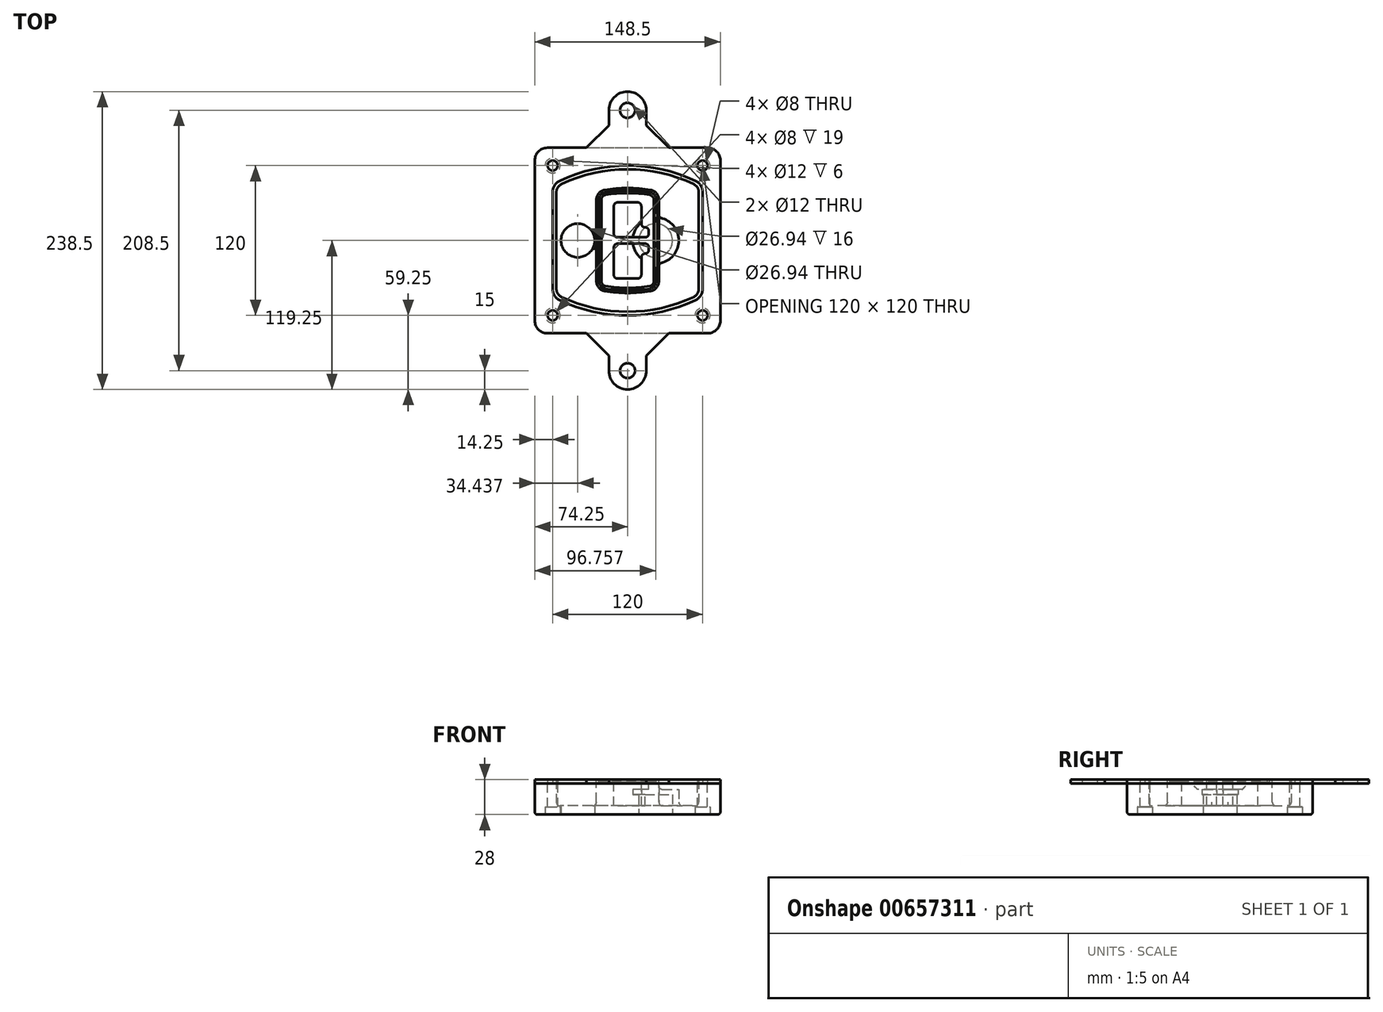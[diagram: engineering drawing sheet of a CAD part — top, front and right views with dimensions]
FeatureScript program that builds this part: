
annotation { "Feature Type Name" : "Feature", "Feature Type Description" : "" }
export const myFeature = defineFeature(function(context is Context, id is Id, definition is map)
    precondition{}
    {
        {
            var Q0;
            Q0=qCreatedBy(makeId("Top.planeOp"),FACE);
            var sketch = newSketch(context, id + "F0", { "sketchPlane" : qUnion([Q0])});
            skPoint(sketch, "E0.rect.middle", {"position": v(0, 0) * mm});
            skLineSegment(sketch, "E1.bottom", {"start": v(-64.25, -74.25) * mm, "end": v(64.25, -74.25) * mm});
            skLineSegment(sketch, "E1.top", {"start": v(-64.25, 74.25) * mm, "end": v(64.25, 74.25) * mm});
            skLineSegment(sketch, "E1.left", {"start": v(-74.25, -64.25) * mm, "end": v(-74.25, 64.25) * mm});
            skLineSegment(sketch, "E1.right", {"start": v(74.25, -64.25) * mm, "end": v(74.25, 64.25) * mm});
            skLineSegment(sketch, "E2", {"start": v(-74.25, 74.25) * mm, "end": v(74.25, -74.25) * mm, "construction": true});
            skLineSegment(sketch, "E3", {"start": v(74.25, 74.25) * mm, "end": v(-74.25, -74.25) * mm, "construction": true});
            skCircle(sketch, "E4", {"center": v(-60, 60) * mm, "radius": 4 * mm});
            skCircle(sketch, "E5", {"center": v(60, 60) * mm, "radius": 4 * mm});
            skCircle(sketch, "E6", {"center": v(60, -60) * mm, "radius": 4 * mm});
            skCircle(sketch, "E7", {"center": v(-60, -60) * mm, "radius": 4 * mm});
            skLineSegment(sketch, "E8", {"start": v(-60, 60) * mm, "end": v(60, 60) * mm, "construction": true});
            skLineSegment(sketch, "E9", {"start": v(60, 60) * mm, "end": v(60, -60) * mm, "construction": true});
            skLineSegment(sketch, "E10", {"start": v(60, -60) * mm, "end": v(-60, -60) * mm, "construction": true});
            skLineSegment(sketch, "E11", {"start": v(-60, -60) * mm, "end": v(-60, 60) * mm, "construction": true});
            skLineSegment(sketch, "E12", {"start": v(-60, 38.83) * mm, "end": v(-60, -38.83) * mm});
            skLineSegment(sketch, "E13", {"start": v(60, 38.83) * mm, "end": v(60, -38.83) * mm});
            skArc(sketch, "E14", {"start": v(54.26, 47.88) * mm, "mid": v(0, 60) * mm, "end": v(-54.26, 47.88) * mm});
            skArc(sketch, "E15", {"start": v(-54.26, -47.88) * mm, "mid": v(0, -60) * mm, "end": v(54.26, -47.88) * mm});
            skLineSegment(sketch, "E16", {"start": v(-60, 0) * mm, "end": v(60, 0) * mm, "construction": true});
            skPoint(sketch, "E17.visualSharp", {"position": v(-60, -45) * mm});
            skArc(sketch, "E17.filletArc", {"start": v(-60, -38.83) * mm, "mid": v(-58.44, -44.2) * mm, "end": v(-54.26, -47.88) * mm});
            skPoint(sketch, "E18.visualSharp", {"position": v(-60, 45) * mm});
            skArc(sketch, "E18.filletArc", {"start": v(-54.26, 47.88) * mm, "mid": v(-58.44, 44.2) * mm, "end": v(-60, 38.83) * mm});
            skPoint(sketch, "E19.visualSharp", {"position": v(60, 45) * mm});
            skArc(sketch, "E19.filletArc", {"start": v(60, 38.83) * mm, "mid": v(58.44, 44.2) * mm, "end": v(54.26, 47.88) * mm});
            skPoint(sketch, "E20.visualSharp", {"position": v(60, -45) * mm});
            skArc(sketch, "E20.filletArc", {"start": v(54.26, -47.88) * mm, "mid": v(58.44, -44.2) * mm, "end": v(60, -38.83) * mm});
            skPoint(sketch, "E21.visualSharp", {"position": v(-74.25, 74.25) * mm});
            skArc(sketch, "E21.filletArc", {"start": v(-64.25, 74.25) * mm, "mid": v(-71.32, 71.32) * mm, "end": v(-74.25, 64.25) * mm});
            skPoint(sketch, "E22.visualSharp", {"position": v(74.25, 74.25) * mm});
            skArc(sketch, "E22.filletArc", {"start": v(74.25, 64.25) * mm, "mid": v(71.32, 71.32) * mm, "end": v(64.25, 74.25) * mm});
            skPoint(sketch, "E23.visualSharp", {"position": v(74.25, -74.25) * mm});
            skArc(sketch, "E23.filletArc", {"start": v(64.25, -74.25) * mm, "mid": v(71.32, -71.32) * mm, "end": v(74.25, -64.25) * mm});
            skPoint(sketch, "E24.visualSharp", {"position": v(-74.25, -74.25) * mm});
            skArc(sketch, "E24.filletArc", {"start": v(-74.25, -64.25) * mm, "mid": v(-71.32, -71.32) * mm, "end": v(-64.25, -74.25) * mm});
            skArc(sketch, "E25.0", {"start": v(57, 38.83) * mm, "mid": v(55.9, 42.58) * mm, "end": v(52.98, 45.17) * mm});
            skLineSegment(sketch, "E25.1", {"start": v(57, 38.83) * mm, "end": v(57, -38.83) * mm});
            skArc(sketch, "E25.2", {"start": v(52.98, -45.17) * mm, "mid": v(55.9, -42.58) * mm, "end": v(57, -38.83) * mm});
            skArc(sketch, "E25.3", {"start": v(-52.98, -45.17) * mm, "mid": v(0, -57) * mm, "end": v(52.98, -45.17) * mm});
            skArc(sketch, "E25.4", {"start": v(-57, -38.83) * mm, "mid": v(-55.9, -42.58) * mm, "end": v(-52.98, -45.17) * mm});
            skArc(sketch, "E25.5", {"start": v(52.98, 45.17) * mm, "mid": v(0, 57) * mm, "end": v(-52.98, 45.17) * mm});
            skLineSegment(sketch, "E25.6", {"start": v(-57, 38.83) * mm, "end": v(-57, -38.83) * mm});
            skArc(sketch, "E25.7", {"start": v(-52.98, 45.17) * mm, "mid": v(-55.9, 42.58) * mm, "end": v(-57, 38.83) * mm});
            skArc(sketch, "E26.0", {"start": v(-55.96, 51.5) * mm, "mid": v(-61.82, 46.33) * mm, "end": v(-64, 38.83) * mm});
            skArc(sketch, "E26.1", {"start": v(55.96, 51.5) * mm, "mid": v(0, 64) * mm, "end": v(-55.96, 51.5) * mm});
            skArc(sketch, "E26.2", {"start": v(64, 38.83) * mm, "mid": v(61.82, 46.33) * mm, "end": v(55.96, 51.5) * mm});
            skLineSegment(sketch, "E26.3", {"start": v(64, 38.83) * mm, "end": v(64, -38.83) * mm});
            skArc(sketch, "E26.4", {"start": v(55.96, -51.5) * mm, "mid": v(61.82, -46.33) * mm, "end": v(64, -38.83) * mm});
            skLineSegment(sketch, "E26.5", {"start": v(-64, 38.83) * mm, "end": v(-64, -38.83) * mm});
            skArc(sketch, "E26.6", {"start": v(-55.96, -51.5) * mm, "mid": v(0, -64) * mm, "end": v(55.96, -51.5) * mm});
            skArc(sketch, "E26.7", {"start": v(-64, -38.83) * mm, "mid": v(-61.82, -46.33) * mm, "end": v(-55.96, -51.5) * mm});
            skLineSegment(sketch, "E27", {"start": v(0, 74.25) * mm, "end": v(0, 104.25) * mm, "construction": true});
            skCircle(sketch, "E28", {"center": v(0, 104.25) * mm, "radius": 6 * mm});
            skArc(sketch, "E29", {"start": v(-15, 104.25) * mm, "mid": v(0, 119.25) * mm, "end": v(15, 104.25) * mm});
            skLineSegment(sketch, "E30", {"start": v(-15, 104.25) * mm, "end": v(-15, 92.25) * mm});
            skLineSegment(sketch, "E31", {"start": v(15, 104.25) * mm, "end": v(15, 92.25) * mm});
            skLineSegment(sketch, "E32", {"start": v(-15, 92.25) * mm, "end": v(-33, 74.25) * mm});
            skLineSegment(sketch, "E33", {"start": v(15, 92.25) * mm, "end": v(33, 74.25) * mm});
            skLineSegment(sketch, "E34", {"start": v(0, -74.25) * mm, "end": v(0, -104.25) * mm, "construction": true});
            skCircle(sketch, "E35", {"center": v(0, -104.25) * mm, "radius": 6 * mm});
            skArc(sketch, "E36", {"start": v(15, -104.25) * mm, "mid": v(0, -119.25) * mm, "end": v(-15, -104.25) * mm});
            skLineSegment(sketch, "E37", {"start": v(15, -104.25) * mm, "end": v(15, -92.25) * mm});
            skLineSegment(sketch, "E38", {"start": v(-15, -104.25) * mm, "end": v(-15, -92.25) * mm});
            skLineSegment(sketch, "E39", {"start": v(15, -92.25) * mm, "end": v(33, -74.25) * mm});
            skLineSegment(sketch, "E40", {"start": v(-15, -92.25) * mm, "end": v(-33, -74.25) * mm});
            skSolve(sketch);
        }
        {
            var Q0;
            Q0=makeQuery(id+"F0.imprint","IMPRINT",FACE,{"disambiguationData":[TD([[makeQuery(id+"F0.imprint","IMPRINT",EDGE,{"derivedFrom":sQuery(id+"F0.wireOp",EDGE,"E1.bottom")}),1.0]])]});
            var Q1;
            Q1=makeQuery(id+"F0.imprint","IMPRINT",FACE,{"disambiguationData":[TD([[makeQuery(id+"F0.imprint","IMPRINT",EDGE,{"derivedFrom":sQuery(id+"F0.wireOp",EDGE,"E12")}),1.0]])]});
            var Q2;
            Q2=makeQuery(id+"F0.imprint","IMPRINT",FACE,{"disambiguationData":[TD([[makeQuery(id+"F0.imprint","IMPRINT",EDGE,{"derivedFrom":sQuery(id+"F0.wireOp",EDGE,"E25.0")}),1.0]])]});
            var Q3;
            Q3=makeQuery(id+"F0.imprint","IMPRINT",FACE,{"disambiguationData":[TD([[makeQuery(id+"F0.imprint","IMPRINT",EDGE,{"derivedFrom":sQuery(id+"F0.wireOp",EDGE,"E12")}),-1.0]])]});
            extrude(context, id + "F1", {"entities" : qUnion([Q0, Q1, Q2, Q3]), "oppositeDirection" : true, "depth" : 25 * mm});
        }
        {
            var Q0;
            Q0=makeQuery(id+"F0.imprint","IMPRINT",FACE,{"disambiguationData":[TD([[makeQuery(id+"F0.imprint","IMPRINT",EDGE,{"derivedFrom":sQuery(id+"F0.wireOp",EDGE,"E12")}),1.0]])]});
            extrude(context, id + "F2", {"entities" : qUnion([Q0]), "operationType" : NewBodyOperationType.ADD, "depth" : 3 * mm});
        }
        {
            var Q0;
            Q0=makeQuery(id+"F0.imprint","IMPRINT",FACE,{"disambiguationData":[TD([[makeQuery(id+"F0.imprint","IMPRINT",EDGE,{"derivedFrom":sQuery(id+"F0.wireOp",EDGE,"E25.0")}),1.0]])]});
            extrude(context, id + "F3", {"entities" : qUnion([Q0]), "operationType" : NewBodyOperationType.REMOVE, "oppositeDirection" : true, "depth" : 18 * mm});
        }
        {
            var Q0;
            Q0=makeQuery(id+"F2.opExtrude","CAP_FACE",FACE,{"disambiguationData":[OSD([sQuery(id+"F0.wireOp",EDGE,"E12"),sQuery(id+"F0.wireOp",EDGE,"E13"),sQuery(id+"F0.wireOp",EDGE,"E14"),sQuery(id+"F0.wireOp",EDGE,"E15"),sQuery(id+"F0.wireOp",EDGE,"E17.filletArc"),sQuery(id+"F0.wireOp",EDGE,"E18.filletArc"),sQuery(id+"F0.wireOp",EDGE,"E19.filletArc"),sQuery(id+"F0.wireOp",EDGE,"E20.filletArc"),sQuery(id+"F0.wireOp",EDGE,"E25.0"),sQuery(id+"F0.wireOp",EDGE,"E25.1"),sQuery(id+"F0.wireOp",EDGE,"E25.2"),sQuery(id+"F0.wireOp",EDGE,"E25.3"),sQuery(id+"F0.wireOp",EDGE,"E25.4"),sQuery(id+"F0.wireOp",EDGE,"E25.5"),sQuery(id+"F0.wireOp",EDGE,"E25.6"),sQuery(id+"F0.wireOp",EDGE,"E25.7")])],"isStart":false});
            var sketch = newSketch(context, id + "F4", { "sketchPlane" : qUnion([Q0])});
            skArc(sketch, "E41.0", {"start": v(-18.34, -40.45) * mm, "mid": v(0, -42) * mm, "end": v(18.34, -40.45) * mm});
            skArc(sketch, "E42.0", {"start": v(18.34, 40.45) * mm, "mid": v(0, 42) * mm, "end": v(-18.34, 40.45) * mm});
            skLineSegment(sketch, "E43", {"start": v(-25, 32.57) * mm, "end": v(-25, -32.57) * mm});
            skLineSegment(sketch, "E44", {"start": v(25, 32.57) * mm, "end": v(25, -32.57) * mm});
            skLineSegment(sketch, "E45", {"start": v(-25, 39.1) * mm, "end": v(25, 39.1) * mm, "construction": true});
            skLineSegment(sketch, "E46", {"start": v(-25, -39.1) * mm, "end": v(25, -39.1) * mm, "construction": true});
            skPoint(sketch, "E47.visualSharp", {"position": v(-25, 39.1) * mm});
            skArc(sketch, "E47.filletArc", {"start": v(-18.34, 40.45) * mm, "mid": v(-23.11, 37.73) * mm, "end": v(-25, 32.57) * mm});
            skPoint(sketch, "E48.visualSharp", {"position": v(25, 39.1) * mm});
            skArc(sketch, "E48.filletArc", {"start": v(25, 32.57) * mm, "mid": v(23.11, 37.73) * mm, "end": v(18.34, 40.45) * mm});
            skPoint(sketch, "E49.visualSharp", {"position": v(25, -39.1) * mm});
            skArc(sketch, "E49.filletArc", {"start": v(18.34, -40.45) * mm, "mid": v(23.11, -37.73) * mm, "end": v(25, -32.57) * mm});
            skPoint(sketch, "E50.visualSharp", {"position": v(-25, -39.1) * mm});
            skArc(sketch, "E50.filletArc", {"start": v(-25, -32.57) * mm, "mid": v(-23.11, -37.73) * mm, "end": v(-18.34, -40.45) * mm});
            skArc(sketch, "E51.0", {"start": v(52.98, 45.17) * mm, "mid": v(0, 57) * mm, "end": v(-52.98, 45.17) * mm});
            skArc(sketch, "E51.1", {"start": v(-52.98, 45.17) * mm, "mid": v(-55.9, 42.58) * mm, "end": v(-57, 38.83) * mm});
            skLineSegment(sketch, "E51.2", {"start": v(-57, 38.83) * mm, "end": v(-57, -38.83) * mm});
            skArc(sketch, "E51.3", {"start": v(-57, -38.83) * mm, "mid": v(-55.9, -42.58) * mm, "end": v(-52.98, -45.17) * mm});
            skArc(sketch, "E51.4", {"start": v(-52.98, -45.17) * mm, "mid": v(0, -57) * mm, "end": v(52.98, -45.17) * mm});
            skArc(sketch, "E51.5", {"start": v(52.98, -45.17) * mm, "mid": v(55.9, -42.58) * mm, "end": v(57, -38.83) * mm});
            skLineSegment(sketch, "E51.6", {"start": v(57, 38.83) * mm, "end": v(57, -38.83) * mm});
            skArc(sketch, "E51.7", {"start": v(57, 38.83) * mm, "mid": v(55.9, 42.58) * mm, "end": v(52.98, 45.17) * mm});
            skLineSegment(sketch, "E52.0", {"start": v(23, 32.57) * mm, "end": v(23, -32.57) * mm});
            skArc(sketch, "E52.1", {"start": v(18, -38.48) * mm, "mid": v(21.58, -36.44) * mm, "end": v(23, -32.57) * mm});
            skArc(sketch, "E52.2", {"start": v(-18, -38.48) * mm, "mid": v(0, -40) * mm, "end": v(18, -38.48) * mm});
            skArc(sketch, "E52.3", {"start": v(-23, -32.57) * mm, "mid": v(-21.58, -36.44) * mm, "end": v(-18, -38.48) * mm});
            skLineSegment(sketch, "E52.4", {"start": v(-23, 32.57) * mm, "end": v(-23, -32.57) * mm});
            skArc(sketch, "E52.5", {"start": v(23, 32.57) * mm, "mid": v(21.58, 36.44) * mm, "end": v(18, 38.48) * mm});
            skArc(sketch, "E52.6", {"start": v(-18, 38.48) * mm, "mid": v(-21.58, 36.44) * mm, "end": v(-23, 32.57) * mm});
            skArc(sketch, "E52.7", {"start": v(18, 38.48) * mm, "mid": v(0, 40) * mm, "end": v(-18, 38.48) * mm});
            skArc(sketch, "E53.0", {"start": v(21, 32.57) * mm, "mid": v(20.06, 35.15) * mm, "end": v(17.67, 36.5) * mm});
            skLineSegment(sketch, "E53.1", {"start": v(21, 32.57) * mm, "end": v(21, -32.57) * mm});
            skArc(sketch, "E53.2", {"start": v(17.67, -36.5) * mm, "mid": v(20.06, -35.15) * mm, "end": v(21, -32.57) * mm});
            skArc(sketch, "E53.3", {"start": v(-17.67, -36.5) * mm, "mid": v(0, -38) * mm, "end": v(17.67, -36.5) * mm});
            skArc(sketch, "E53.4", {"start": v(-21, -32.57) * mm, "mid": v(-20.06, -35.15) * mm, "end": v(-17.67, -36.5) * mm});
            skArc(sketch, "E53.5", {"start": v(17.67, 36.5) * mm, "mid": v(0, 38) * mm, "end": v(-17.67, 36.5) * mm});
            skLineSegment(sketch, "E53.6", {"start": v(-21, 32.57) * mm, "end": v(-21, -32.57) * mm});
            skArc(sketch, "E53.7", {"start": v(-17.67, 36.5) * mm, "mid": v(-20.06, 35.15) * mm, "end": v(-21, 32.57) * mm});
            skLineSegment(sketch, "E54", {"start": v(-25, 0) * mm, "end": v(25, 0) * mm, "construction": true});
            skLineSegment(sketch, "E55", {"start": v(-11, 5.5) * mm, "end": v(-11, 27.5) * mm});
            skLineSegment(sketch, "E56", {"start": v(-8, 30.5) * mm, "end": v(8, 30.5) * mm});
            skLineSegment(sketch, "E57", {"start": v(11, 27.5) * mm, "end": v(11, 13.5) * mm});
            skLineSegment(sketch, "E58", {"start": v(14, 10.5) * mm, "end": v(14, 10.5) * mm});
            skLineSegment(sketch, "E59", {"start": v(17, 7.5) * mm, "end": v(17, 5.5) * mm});
            skLineSegment(sketch, "E60", {"start": v(14, 2.5) * mm, "end": v(-8, 2.5) * mm});
            skPoint(sketch, "E61.visualSharp", {"position": v(-11, 30.5) * mm});
            skArc(sketch, "E61.filletArc", {"start": v(-8, 30.5) * mm, "mid": v(-10.12, 29.62) * mm, "end": v(-11, 27.5) * mm});
            skPoint(sketch, "E62.visualSharp", {"position": v(11, 30.5) * mm});
            skArc(sketch, "E62.filletArc", {"start": v(11, 27.5) * mm, "mid": v(10.12, 29.62) * mm, "end": v(8, 30.5) * mm});
            skPoint(sketch, "E63.visualSharp", {"position": v(11, 10.5) * mm});
            skArc(sketch, "E63.filletArc", {"start": v(11, 13.5) * mm, "mid": v(11.88, 11.38) * mm, "end": v(14, 10.5) * mm});
            skPoint(sketch, "E64.visualSharp", {"position": v(17, 10.5) * mm});
            skArc(sketch, "E64.filletArc", {"start": v(17, 7.5) * mm, "mid": v(16.12, 9.62) * mm, "end": v(14, 10.5) * mm});
            skPoint(sketch, "E65.visualSharp", {"position": v(17, 2.5) * mm});
            skArc(sketch, "E65.filletArc", {"start": v(14, 2.5) * mm, "mid": v(16.12, 3.38) * mm, "end": v(17, 5.5) * mm});
            skPoint(sketch, "E66.visualSharp", {"position": v(-11, 2.5) * mm});
            skArc(sketch, "E66.filletArc", {"start": v(-11, 5.5) * mm, "mid": v(-10.12, 3.38) * mm, "end": v(-8, 2.5) * mm});
            skLineSegment(sketch, "E67.0.MirrorCS", {"start": v(14, -2.5) * mm, "end": v(-8, -2.5) * mm});
            skArc(sketch, "E68.0.MirrorCS", {"start": v(-11, -5.5) * mm, "mid": v(-10.12, -3.38) * mm, "end": v(-8, -2.5) * mm});
            skLineSegment(sketch, "E69.0.MirrorCS", {"start": v(-11, -5.5) * mm, "end": v(-11, -27.5) * mm});
            skArc(sketch, "E70.0.MirrorCS", {"start": v(-8, -30.5) * mm, "mid": v(-10.12, -29.62) * mm, "end": v(-11, -27.5) * mm});
            skLineSegment(sketch, "E71.0.MirrorCS", {"start": v(-8, -30.5) * mm, "end": v(8, -30.5) * mm});
            skArc(sketch, "E72.0.MirrorCS", {"start": v(11, -27.5) * mm, "mid": v(10.12, -29.62) * mm, "end": v(8, -30.5) * mm});
            skLineSegment(sketch, "E73.0.MirrorCS", {"start": v(11, -27.5) * mm, "end": v(11, -13.5) * mm});
            skArc(sketch, "E74.0.MirrorCS", {"start": v(11, -13.5) * mm, "mid": v(11.88, -11.38) * mm, "end": v(14, -10.5) * mm});
            skArc(sketch, "E75.0.MirrorCS", {"start": v(17, -7.5) * mm, "mid": v(16.12, -9.62) * mm, "end": v(14, -10.5) * mm});
            skLineSegment(sketch, "E76.0.MirrorCS", {"start": v(17, -7.5) * mm, "end": v(17, -5.5) * mm});
            skArc(sketch, "E77.0.MirrorCS", {"start": v(14, -2.5) * mm, "mid": v(16.12, -3.38) * mm, "end": v(17, -5.5) * mm});
            skSolve(sketch);
        }
        {
            var Q0;
            Q0=makeQuery(id+"F4.imprint","IMPRINT",FACE,{"disambiguationData":[TD([[makeQuery(id+"F4.imprint","IMPRINT",EDGE,{"derivedFrom":sQuery(id+"F4.wireOp",EDGE,"E41.0")}),1.0]])]});
            var Q1;
            Q1=makeQuery(id+"F4.imprint","IMPRINT",FACE,{"disambiguationData":[TD([[makeQuery(id+"F4.imprint","IMPRINT",EDGE,{"derivedFrom":sQuery(id+"F4.wireOp",EDGE,"E52.0")}),-1.0]])]});
            var Q2;
            Q2=makeQuery(id+"F4.imprint","IMPRINT",FACE,{"disambiguationData":[TD([[makeQuery(id+"F4.imprint","IMPRINT",EDGE,{"derivedFrom":sQuery(id+"F4.wireOp",EDGE,"E53.0")}),1.0]])]});
            extrude(context, id + "F5", {"entities" : qUnion([Q0, Q1, Q2]), "operationType" : NewBodyOperationType.ADD, "endBound" : BoundingType.UP_TO_NEXT, "oppositeDirection" : true, "depth" : 25 * mm});
        }
        {
            var Q0;
            Q0=makeQuery(id+"F4.imprint","IMPRINT",FACE,{"disambiguationData":[TD([[makeQuery(id+"F4.imprint","IMPRINT",EDGE,{"derivedFrom":sQuery(id+"F4.wireOp",EDGE,"E52.0")}),-1.0]])]});
            extrude(context, id + "F6", {"entities" : qUnion([Q0]), "operationType" : NewBodyOperationType.REMOVE, "oppositeDirection" : true, "depth" : 2 * mm});
        }
        {
            var Q0;
            Q0=makeQuery(id+"F1.opExtrude","CAP_FACE",FACE,{"disambiguationData":[OSD([sQuery(id+"F0.wireOp",EDGE,"E1.bottom"),sQuery(id+"F0.wireOp",EDGE,"E1.top"),sQuery(id+"F0.wireOp",EDGE,"E1.left"),sQuery(id+"F0.wireOp",EDGE,"E1.right"),sQuery(id+"F0.wireOp",EDGE,"E4"),sQuery(id+"F0.wireOp",EDGE,"E5"),sQuery(id+"F0.wireOp",EDGE,"E6"),sQuery(id+"F0.wireOp",EDGE,"E7"),sQuery(id+"F0.wireOp",EDGE,"E21.filletArc"),sQuery(id+"F0.wireOp",EDGE,"E22.filletArc"),sQuery(id+"F0.wireOp",EDGE,"E23.filletArc"),sQuery(id+"F0.wireOp",EDGE,"E24.filletArc")])],"isStart":false});
            var sketch = newSketch(context, id + "F7", { "sketchPlane" : qUnion([Q0])});
            skCircle(sketch, "E78", {"center": v(22.5, 0) * mm, "radius": 13.47 * mm});
            skCircle(sketch, "E79", {"center": v(-39.81, 0) * mm, "radius": 13.47 * mm});
            skLineSegment(sketch, "E80", {"start": v(74.25, 0) * mm, "end": v(-74.25, 0) * mm});
            skCircle(sketch, "E81", {"center": v(22.5, 0) * mm, "radius": 18.47 * mm});
            skCircle(sketch, "E82", {"center": v(60, -60) * mm, "radius": 6 * mm});
            skCircle(sketch, "E83", {"center": v(-60, -60) * mm, "radius": 6 * mm});
            skCircle(sketch, "E84", {"center": v(-60, 60) * mm, "radius": 6 * mm});
            skCircle(sketch, "E85", {"center": v(60, 60) * mm, "radius": 6 * mm});
            skSolve(sketch);
        }
        {
            var Q0;
            {var subQ1=sQuery(id+"F7.wireOp",EDGE,"E80");var subQ4=sQuery(id+"F7.wireOp",EDGE,"E78");var subQ6=makeQuery(id+"F7.imprint","INTERSECT",VERTEX,{"disambiguationData":[OD(0.0)],"derivedFrom":[subQ4,subQ1]});Q0=makeQuery(id+"F7.imprint","IMPRINT",FACE,{"disambiguationData":[TD([[makeQuery(id+"F7.imprint","IMPRINT",EDGE,{"disambiguationData":[TD([[subQ6,-1.0]])],"derivedFrom":subQ4}),-1.0]])]});}
            var Q1;
            {var subQ0=sQuery(id+"F7.wireOp",EDGE,"E80");var subQ1=sQuery(id+"F7.wireOp",EDGE,"E78");var subQ3=makeQuery(id+"F7.imprint","INTERSECT",VERTEX,{"disambiguationData":[OD(0.0)],"derivedFrom":[subQ1,subQ0]});Q1=makeQuery(id+"F7.imprint","IMPRINT",FACE,{"disambiguationData":[TD([[makeQuery(id+"F7.imprint","IMPRINT",EDGE,{"disambiguationData":[TD([[subQ3,-1.0]])],"derivedFrom":subQ1}),1.0]])]});}
            var Q2;
            {var subQ0=sQuery(id+"F7.wireOp",EDGE,"E80");var subQ1=sQuery(id+"F7.wireOp",EDGE,"E78");var subQ3=makeQuery(id+"F7.imprint","INTERSECT",VERTEX,{"disambiguationData":[OD(0.0)],"derivedFrom":[subQ1,subQ0]});Q2=makeQuery(id+"F7.imprint","IMPRINT",FACE,{"disambiguationData":[TD([[makeQuery(id+"F7.imprint","IMPRINT",EDGE,{"disambiguationData":[TD([[subQ3,1.0]])],"derivedFrom":subQ1}),1.0]])]});}
            var Q3;
            {var subQ1=sQuery(id+"F7.wireOp",EDGE,"E80");var subQ4=sQuery(id+"F7.wireOp",EDGE,"E78");var subQ6=makeQuery(id+"F7.imprint","INTERSECT",VERTEX,{"disambiguationData":[OD(0.0)],"derivedFrom":[subQ4,subQ1]});Q3=makeQuery(id+"F7.imprint","IMPRINT",FACE,{"disambiguationData":[TD([[makeQuery(id+"F7.imprint","IMPRINT",EDGE,{"disambiguationData":[TD([[subQ6,1.0]])],"derivedFrom":subQ4}),-1.0]])]});}
            extrude(context, id + "F8", {"entities" : qUnion([Q0, Q1, Q2, Q3]), "operationType" : NewBodyOperationType.ADD, "oppositeDirection" : true, "depth" : 20 * mm});
        }
        {
            var Q0;
            {var subQ0=sQuery(id+"F7.wireOp",EDGE,"E80");var subQ1=sQuery(id+"F7.wireOp",EDGE,"E78");var subQ3=makeQuery(id+"F7.imprint","INTERSECT",VERTEX,{"disambiguationData":[OD(0.0)],"derivedFrom":[subQ1,subQ0]});Q0=makeQuery(id+"F7.imprint","IMPRINT",FACE,{"disambiguationData":[TD([[makeQuery(id+"F7.imprint","IMPRINT",EDGE,{"disambiguationData":[TD([[subQ3,-1.0]])],"derivedFrom":subQ1}),1.0]])]});}
            var Q1;
            {var subQ0=sQuery(id+"F7.wireOp",EDGE,"E80");var subQ1=sQuery(id+"F7.wireOp",EDGE,"E78");var subQ3=makeQuery(id+"F7.imprint","INTERSECT",VERTEX,{"disambiguationData":[OD(0.0)],"derivedFrom":[subQ1,subQ0]});Q1=makeQuery(id+"F7.imprint","IMPRINT",FACE,{"disambiguationData":[TD([[makeQuery(id+"F7.imprint","IMPRINT",EDGE,{"disambiguationData":[TD([[subQ3,1.0]])],"derivedFrom":subQ1}),1.0]])]});}
            extrude(context, id + "F9", {"entities" : qUnion([Q0, Q1]), "operationType" : NewBodyOperationType.REMOVE, "oppositeDirection" : true, "depth" : 16 * mm});
        }
        {
            var Q0;
            {var subQ0=sQuery(id+"F7.wireOp",EDGE,"E80");var subQ1=sQuery(id+"F7.wireOp",EDGE,"E79");var subQ3=makeQuery(id+"F7.imprint","INTERSECT",VERTEX,{"disambiguationData":[OD(0.0)],"derivedFrom":[subQ1,subQ0]});Q0=makeQuery(id+"F7.imprint","IMPRINT",FACE,{"disambiguationData":[TD([[makeQuery(id+"F7.imprint","IMPRINT",EDGE,{"disambiguationData":[TD([[subQ3,-1.0]])],"derivedFrom":subQ1}),1.0]])]});}
            var Q1;
            {var subQ0=sQuery(id+"F7.wireOp",EDGE,"E80");var subQ1=sQuery(id+"F7.wireOp",EDGE,"E79");var subQ3=makeQuery(id+"F7.imprint","INTERSECT",VERTEX,{"disambiguationData":[OD(0.0)],"derivedFrom":[subQ1,subQ0]});Q1=makeQuery(id+"F7.imprint","IMPRINT",FACE,{"disambiguationData":[TD([[makeQuery(id+"F7.imprint","IMPRINT",EDGE,{"disambiguationData":[TD([[subQ3,1.0]])],"derivedFrom":subQ1}),1.0]])]});}
            extrude(context, id + "F10", {"entities" : qUnion([Q0, Q1]), "operationType" : NewBodyOperationType.REMOVE, "oppositeDirection" : true, "depth" : 25 * mm});
        }
        {
            var Q0;
            Q0=makeQuery(id+"F7.imprint","IMPRINT",FACE,{"disambiguationData":[TD([[makeQuery(id+"F7.imprint","IMPRINT",EDGE,{"derivedFrom":sQuery(id+"F7.wireOp",EDGE,"E82")}),1.0]])]});
            var Q1;
            Q1=makeQuery(id+"F7.imprint","IMPRINT",FACE,{"disambiguationData":[TD([[makeQuery(id+"F7.imprint","IMPRINT",EDGE,{"derivedFrom":makeQuery(id+"F1.opExtrude","CAP_EDGE",EDGE,{"disambiguationData":[OSD([sQuery(id+"F0.wireOp",EDGE,"E5")])],"isStart":false})}),-1.0]])]});
            var Q2;
            Q2=makeQuery(id+"F7.imprint","IMPRINT",FACE,{"disambiguationData":[TD([[makeQuery(id+"F7.imprint","IMPRINT",EDGE,{"derivedFrom":sQuery(id+"F7.wireOp",EDGE,"E83")}),1.0]])]});
            var Q3;
            Q3=makeQuery(id+"F7.imprint","IMPRINT",FACE,{"disambiguationData":[TD([[makeQuery(id+"F7.imprint","IMPRINT",EDGE,{"derivedFrom":makeQuery(id+"F1.opExtrude","CAP_EDGE",EDGE,{"disambiguationData":[OSD([sQuery(id+"F0.wireOp",EDGE,"E4")])],"isStart":false})}),-1.0]])]});
            var Q4;
            Q4=makeQuery(id+"F7.imprint","IMPRINT",FACE,{"disambiguationData":[TD([[makeQuery(id+"F7.imprint","IMPRINT",EDGE,{"derivedFrom":sQuery(id+"F7.wireOp",EDGE,"E84")}),1.0]])]});
            var Q5;
            Q5=makeQuery(id+"F7.imprint","IMPRINT",FACE,{"disambiguationData":[TD([[makeQuery(id+"F7.imprint","IMPRINT",EDGE,{"derivedFrom":makeQuery(id+"F1.opExtrude","CAP_EDGE",EDGE,{"disambiguationData":[OSD([sQuery(id+"F0.wireOp",EDGE,"E7")])],"isStart":false})}),-1.0]])]});
            var Q6;
            Q6=makeQuery(id+"F7.imprint","IMPRINT",FACE,{"disambiguationData":[TD([[makeQuery(id+"F7.imprint","IMPRINT",EDGE,{"derivedFrom":sQuery(id+"F7.wireOp",EDGE,"E85")}),1.0]])]});
            var Q7;
            Q7=makeQuery(id+"F7.imprint","IMPRINT",FACE,{"disambiguationData":[TD([[makeQuery(id+"F7.imprint","IMPRINT",EDGE,{"derivedFrom":makeQuery(id+"F1.opExtrude","CAP_EDGE",EDGE,{"disambiguationData":[OSD([sQuery(id+"F0.wireOp",EDGE,"E6")])],"isStart":false})}),-1.0]])]});
            extrude(context, id + "F11", {"entities" : qUnion([Q0, Q1, Q2, Q3, Q4, Q5, Q6, Q7]), "operationType" : NewBodyOperationType.REMOVE, "oppositeDirection" : true, "depth" : 6 * mm});
        }
        {
            var Q0;
            Q0=makeQuery(id+"F9.boolean.opBoolean","COPY",FACE,{"derivedFrom":makeQuery(id+"F9.opExtrude","CAP_FACE",FACE,{"disambiguationData":[OSD([sQuery(id+"F7.wireOp",EDGE,"E78")])],"isStart":false})});
            var sketch = newSketch(context, id + "F12", { "sketchPlane" : qUnion([Q0])});
            skArc(sketch, "E86.0", {"start": v(11, 14.45) * mm, "mid": v(6.45, 9.13) * mm, "end": v(4.2, 2.5) * mm});
            skArc(sketch, "E86.1", {"start": v(4.2, -2.5) * mm, "mid": v(6.45, -9.13) * mm, "end": v(11, -14.45) * mm});
            skLineSegment(sketch, "E87", {"start": v(4.2, -2.5) * mm, "end": v(14, -2.5) * mm});
            skLineSegment(sketch, "E88.0", {"start": v(14, 2.5) * mm, "end": v(4.2, 2.5) * mm});
            skArc(sketch, "E88.1", {"start": v(14, 2.5) * mm, "mid": v(16.12, 3.38) * mm, "end": v(17, 5.5) * mm});
            skLineSegment(sketch, "E88.2", {"start": v(17, 7.5) * mm, "end": v(17, 5.5) * mm});
            skArc(sketch, "E88.3", {"start": v(17, 7.5) * mm, "mid": v(16.12, 9.62) * mm, "end": v(14, 10.5) * mm});
            skArc(sketch, "E88.4", {"start": v(11, 13.5) * mm, "mid": v(11.88, 11.38) * mm, "end": v(14, 10.5) * mm});
            skLineSegment(sketch, "E88.5", {"start": v(11, 14.45) * mm, "end": v(11, 13.5) * mm});
            skLineSegment(sketch, "E88.7", {"start": v(14, -2.5) * mm, "end": v(4.2, -2.5) * mm});
            skArc(sketch, "E88.8", {"start": v(14, -2.5) * mm, "mid": v(16.12, -3.38) * mm, "end": v(17, -5.5) * mm});
            skLineSegment(sketch, "E88.9", {"start": v(17, -7.5) * mm, "end": v(17, -5.5) * mm});
            skArc(sketch, "E88.10", {"start": v(17, -7.5) * mm, "mid": v(16.12, -9.62) * mm, "end": v(14, -10.5) * mm});
            skArc(sketch, "E88.11", {"start": v(11, -13.5) * mm, "mid": v(11.88, -11.38) * mm, "end": v(14, -10.5) * mm});
            skLineSegment(sketch, "E88.12", {"start": v(11, -14.45) * mm, "end": v(11, -13.5) * mm});
            skPoint(sketch, "E89.orphan", {"position": v(11, -27.5) * mm});
            skPoint(sketch, "E90.orphan", {"position": v(-8, -2.5) * mm});
            skPoint(sketch, "E91.orphan", {"position": v(-8, 2.5) * mm});
            skPoint(sketch, "E92.orphan", {"position": v(11, 27.5) * mm});
            skSolve(sketch);
        }
        {
            var Q0;
            {var subQ7=sQuery(id+"F12.wireOp",EDGE,"E86.0");var subQ14=sQuery(id+"F12.wireOp",EDGE,"E86.1");var subQ16=sQuery(id+"F12.wireOp",EDGE,"E88.1");var subQ18=sQuery(id+"F12.wireOp",EDGE,"E88.8");Q0=qUnion([makeQuery(id+"F12.imprint","IMPRINT",FACE,{"disambiguationData":[TD([[makeQuery(id+"F12.imprint","IMPRINT",EDGE,{"derivedFrom":subQ7}),1.0]])]}),makeQuery(id+"F12.imprint","IMPRINT",FACE,{"disambiguationData":[TD([[makeQuery(id+"F12.imprint","IMPRINT",EDGE,{"derivedFrom":subQ14}),1.0]])]}),makeQuery(id+"F12.imprint","IMPRINT",FACE,{"disambiguationData":[TD([[makeQuery(id+"F12.imprint","IMPRINT",EDGE,{"derivedFrom":subQ16}),1.0]])]}),makeQuery(id+"F12.imprint","IMPRINT",FACE,{"disambiguationData":[TD([[makeQuery(id+"F12.imprint","IMPRINT",EDGE,{"derivedFrom":subQ18}),-1.0]])]})]);}
            var Q1;
            Q1=makeQuery(id+"F5.boolean.opBoolean","SPLIT",FACE,{"disambiguationData":[TD([makeQuery(id+"F5.opExtrude","SWEPT_FACE",FACE,{"disambiguationData":[OSD([sQuery(id+"F4.wireOp",EDGE,"E55")])]})])],"derivedFrom":makeQuery(id+"F3.boolean.opBoolean","COPY",FACE,{"derivedFrom":makeQuery(id+"F3.opExtrude","CAP_FACE",FACE,{"disambiguationData":[OSD([sQuery(id+"F0.wireOp",EDGE,"E25.0"),sQuery(id+"F0.wireOp",EDGE,"E25.1"),sQuery(id+"F0.wireOp",EDGE,"E25.2"),sQuery(id+"F0.wireOp",EDGE,"E25.3"),sQuery(id+"F0.wireOp",EDGE,"E25.4"),sQuery(id+"F0.wireOp",EDGE,"E25.5"),sQuery(id+"F0.wireOp",EDGE,"E25.6"),sQuery(id+"F0.wireOp",EDGE,"E25.7")])],"isStart":false})})});
            extrude(context, id + "F13", {"entities" : qUnion([Q0]), "operationType" : NewBodyOperationType.REMOVE, "endBound" : BoundingType.UP_TO_SURFACE, "endBoundEntityFace" : qUnion([Q1]), "depth" : 25 * mm});
        }
        {
            var Q0;
            Q0=makeQuery(id+"F3.boolean.opBoolean","COPY",EDGE,{"derivedFrom":makeQuery(id+"F3.opExtrude","CAP_EDGE",EDGE,{"disambiguationData":[OSD([sQuery(id+"F0.wireOp",EDGE,"E25.6")])],"isStart":false})});
            var Q1;
            Q1=makeQuery(id+"F8.boolean.opBoolean","INTERSECT",EDGE,{"derivedFrom":[makeQuery(id+"F5.opExtrude","SWEPT_FACE",FACE,{"disambiguationData":[OSD([sQuery(id+"F4.wireOp",EDGE,"E44")])]}),makeQuery(id+"F8.opExtrude","CAP_FACE",FACE,{"disambiguationData":[OSD([sQuery(id+"F7.wireOp",EDGE,"E81")])],"isStart":false})]});
            var Q2;
            Q2=makeQuery(id+"F8.boolean.opBoolean","INTERSECT",EDGE,{"disambiguationData":[OD(1.0)],"derivedFrom":[makeQuery(id+"F5.opExtrude","SWEPT_FACE",FACE,{"disambiguationData":[OSD([sQuery(id+"F4.wireOp",EDGE,"E44")])]}),makeQuery(id+"F8.opExtrude","SWEPT_FACE",FACE,{"disambiguationData":[OSD([sQuery(id+"F7.wireOp",EDGE,"E81")])]})]});
            var Q3;
            {var subQ0=sQuery(id+"F4.wireOp",EDGE,"E44");Q3=makeQuery(id+"F8.boolean.opBoolean","SPLIT",EDGE,{"disambiguationData":[TD([makeQuery(id+"F5.opExtrude","SWEPT_FACE",FACE,{"disambiguationData":[OSD([sQuery(id+"F4.wireOp",EDGE,"E49.filletArc")])]})])],"derivedFrom":makeQuery(id+"F5.opExtrude","CAP_EDGE",EDGE,{"disambiguationData":[OSD([subQ0])],"isStart":false})});}
            var Q4;
            {var subQ0=sQuery(id+"F0.wireOp",EDGE,"E25.7");var subQ1=sQuery(id+"F0.wireOp",EDGE,"E25.1");var subQ2=sQuery(id+"F0.wireOp",EDGE,"E25.6");var subQ3=sQuery(id+"F0.wireOp",EDGE,"E25.5");var subQ4=sQuery(id+"F0.wireOp",EDGE,"E25.4");var subQ5=sQuery(id+"F0.wireOp",EDGE,"E25.0");var subQ6=sQuery(id+"F0.wireOp",EDGE,"E25.2");var subQ7=sQuery(id+"F0.wireOp",EDGE,"E25.3");Q4=makeQuery(id+"F8.boolean.opBoolean","INTERSECT",EDGE,{"derivedFrom":[makeQuery(id+"F5.boolean.opBoolean","SPLIT",FACE,{"disambiguationData":[TD([makeQuery(id+"F2.opExtrude","SWEPT_FACE",FACE,{"disambiguationData":[OSD([subQ5])]})])],"derivedFrom":makeQuery(id+"F3.boolean.opBoolean","COPY",FACE,{"derivedFrom":makeQuery(id+"F3.opExtrude","CAP_FACE",FACE,{"disambiguationData":[OSD([subQ5,subQ1,subQ6,subQ7,subQ4,subQ3,subQ2,subQ0])],"isStart":false})})}),makeQuery(id+"F8.opExtrude","SWEPT_FACE",FACE,{"disambiguationData":[OSD([sQuery(id+"F7.wireOp",EDGE,"E81")])]})]});}
            var Q5;
            Q5=makeQuery(id+"F8.boolean.opBoolean","INTERSECT",EDGE,{"disambiguationData":[OD(0.0)],"derivedFrom":[makeQuery(id+"F5.opExtrude","SWEPT_FACE",FACE,{"disambiguationData":[OSD([sQuery(id+"F4.wireOp",EDGE,"E44")])]}),makeQuery(id+"F8.opExtrude","SWEPT_FACE",FACE,{"disambiguationData":[OSD([sQuery(id+"F7.wireOp",EDGE,"E81")])]})]});
            fillet(context, id + "F14", {"entities" : qUnion([Q0, Q1, Q2, Q3, Q4, Q5]), "radius" : 3 * mm, "tangentPropagation" : true, "allowEdgeOverflow" : false});
        }
        {
            var Q0;
            Q0=makeQuery(id+"F1.opExtrude","CAP_EDGE",EDGE,{"disambiguationData":[OSD([sQuery(id+"F0.wireOp",EDGE,"E1.bottom")])],"isStart":false});
            fillet(context, id + "F15", {"entities" : qUnion([Q0]), "radius" : 2 * mm, "tangentPropagation" : true, "allowEdgeOverflow" : false});
        }
        {
            var Q0;
            Q0 = qSketchRegion(id + "F0", true);
            var Q1;
            Q1=makeQuery(id+"F0.imprint","IMPRINT",FACE,{"disambiguationData":[TD([[makeQuery(id+"F0.imprint","IMPRINT",EDGE,{"derivedFrom":sQuery(id+"F0.wireOp",EDGE,"E12")}),-1.0]])]});
            var Q2;
            {var subQ0=sQuery(id+"F4.wireOp",EDGE,"E50.filletArc");var subQ1=sQuery(id+"F4.wireOp",EDGE,"E49.filletArc");var subQ2=sQuery(id+"F4.wireOp",EDGE,"E48.filletArc");var subQ3=sQuery(id+"F4.wireOp",EDGE,"E47.filletArc");var subQ4=sQuery(id+"F4.wireOp",EDGE,"E41.0");var subQ5=sQuery(id+"F4.wireOp",EDGE,"E44");var subQ6=sQuery(id+"F4.wireOp",EDGE,"E42.0");var subQ7=sQuery(id+"F4.wireOp",EDGE,"E43");Q2=makeQuery(id+"F6.boolean.opBoolean","SPLIT",FACE,{"disambiguationData":[TD([makeQuery(id+"F5.opExtrude","SWEPT_FACE",FACE,{"disambiguationData":[OSD([subQ4])]})])],"derivedFrom":makeQuery(id+"F5.opExtrude","CAP_FACE",FACE,{"disambiguationData":[OSD([subQ4,subQ6,subQ7,subQ5,subQ3,subQ2,subQ1,subQ0,sQuery(id+"F4.wireOp",EDGE,"E55"),sQuery(id+"F4.wireOp",EDGE,"E56"),sQuery(id+"F4.wireOp",EDGE,"E57"),sQuery(id+"F4.wireOp",EDGE,"E59"),sQuery(id+"F4.wireOp",EDGE,"E60"),sQuery(id+"F4.wireOp",EDGE,"E61.filletArc"),sQuery(id+"F4.wireOp",EDGE,"E62.filletArc"),sQuery(id+"F4.wireOp",EDGE,"E63.filletArc"),sQuery(id+"F4.wireOp",EDGE,"E64.filletArc"),sQuery(id+"F4.wireOp",EDGE,"E65.filletArc"),sQuery(id+"F4.wireOp",EDGE,"E66.filletArc"),sQuery(id+"F4.wireOp",EDGE,"E67.0.MirrorCS"),sQuery(id+"F4.wireOp",EDGE,"E68.0.MirrorCS"),sQuery(id+"F4.wireOp",EDGE,"E69.0.MirrorCS"),sQuery(id+"F4.wireOp",EDGE,"E70.0.MirrorCS"),sQuery(id+"F4.wireOp",EDGE,"E71.0.MirrorCS"),sQuery(id+"F4.wireOp",EDGE,"E72.0.MirrorCS"),sQuery(id+"F4.wireOp",EDGE,"E73.0.MirrorCS"),sQuery(id+"F4.wireOp",EDGE,"E74.0.MirrorCS"),sQuery(id+"F4.wireOp",EDGE,"E75.0.MirrorCS"),sQuery(id+"F4.wireOp",EDGE,"E76.0.MirrorCS"),sQuery(id+"F4.wireOp",EDGE,"E77.0.MirrorCS")])],"isStart":true})});}
            extrude(context, id + "F16", {"entities" : qUnion([Q0, Q1]), "endBound" : BoundingType.UP_TO_SURFACE, "depth" : 25 * mm, "endBoundEntityFace" : qUnion([Q2]), "offsetDistance" : 25 * mm});
        }
    });
